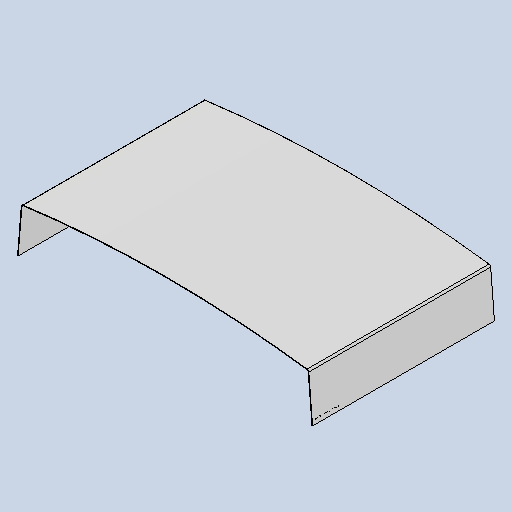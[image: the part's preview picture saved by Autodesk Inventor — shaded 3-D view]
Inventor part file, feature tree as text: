
AUTODESK INVENTOR PART (.ipt)
format: ipt  version: 2025 (Build 290162010, 162A)  size: 306,176 bytes
history: native  units: mm
features: other x4, sheet_metal_op x3, sketch x2, mirror x1
ambient origin geometry x8: Origin, YZ Plane, XZ Plane, XY Plane, X Axis, Y Axis, Z Axis, Center Point
bodies: Body1 (feature_tree)
feature tree (10):
  sheet_metal_op  "Contour Flange2"
  mirror  "Mirror2"
  other  "Mark1"
  other  "A-Side Definition"
  sketch  "Sketch1"  dims[d36=3.0mm]
  other  "Plate2"
  sheet_metal_op  "Bend2"
  sheet_metal_op  "Corner2"
  sketch  "Sketch2"  dims[d37=3.0mm d38=1.5mm d39=6.0mm d40=5.0mm d41=950.0mm d42=5.0mm d43=3.0mm d44=12.0mm d45=3.0mm d46=5.0mm d54=1500.0mm d55=2700.0mm d58=2100.0mm d65=8.0mm d66=8.0mm d78=3.0mm d80=3.0mm d83=8.0mm d113=50.0mm d114=50.0mm d115=3.0mm d121=10.0mm d122=241.9mm d124=16.546129mm]
  other  "Definition1"
